# Revit family: Radar Pedagogico
name_source: partatom
category: Furniture
units: mm (PartAtom-declared; Revit-internal decimal feet)

## family parameters
Always vertical = Yes
Cut with Voids When Loaded = No
OmniClass Number = 23.40.20.00
OmniClass Title = General Furniture and Specialties
Room Calculation Point = No
Shared = No
Work Plane-Based = No

## types (1)
- Radar Pedagogico-SRAD-620mm
    A = 0.62 m
    B = 0.62 m
    C = 0.04 m
    D = 0.455 m
    Default Elevation = 0 m
    Description = El radar pedagógico de BENITO sirve para disuadir a los usuarios que circulan por encima del límite
establecido, mostrándoles que lo están infringiendo. Está demostrado que a pesar de no ser un radar
sancionador, su efectividad es muy buena. Además es una medida menos agresiva para los vecinos que
otros sistemas de reducción de velocidad como son las bandas reductoras y otros obstáculos que suelen
suponer un inconveniente para los usuarios más recurrentes.
    E = 0.34 m
    Fabricante = BENITO URBAN SL
    Ficha_Tecnica = https://www.benito.com
    Material = <By Category>
    Referencia = SRAD
    URL_Producto = https://www.benito.com

## geometry (parser evidence)
native form markers: Blend x8, Sweep x2
no freeform markers — native parametric forms only
